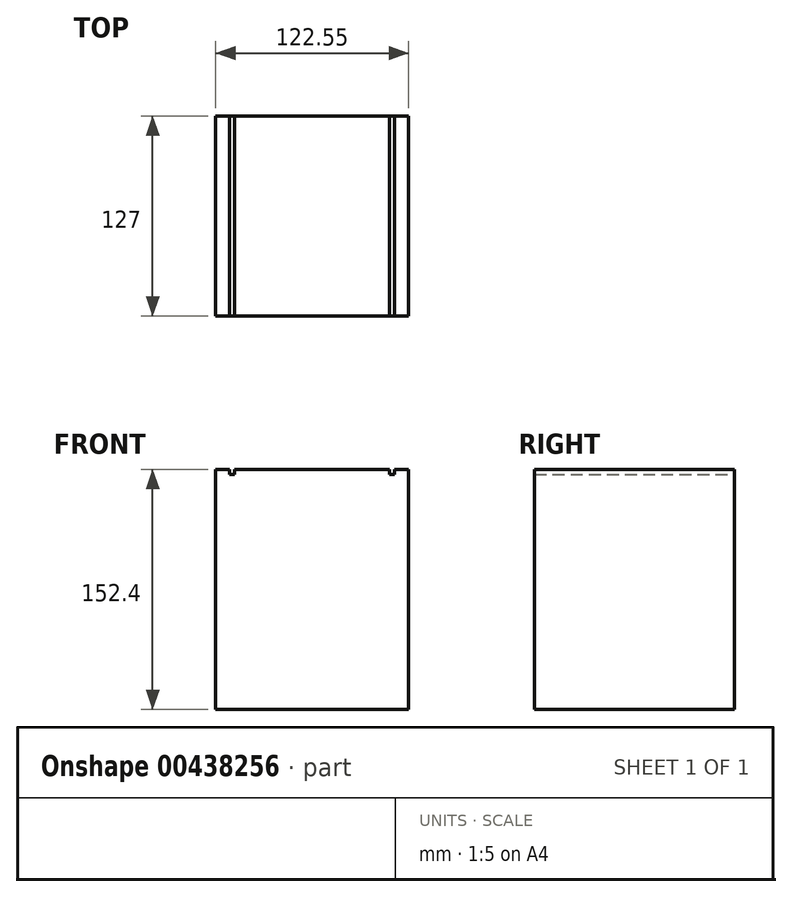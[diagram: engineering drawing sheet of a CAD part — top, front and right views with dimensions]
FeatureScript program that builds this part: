
annotation { "Feature Type Name" : "Feature", "Feature Type Description" : "" }
export const myFeature = defineFeature(function(context is Context, id is Id, definition is map)
    precondition{}
    {
        {
            var Q0;
            Q0=qCreatedBy(makeId("Front.planeOp"),FACE);
            var sketch = newSketch(context, id + "F0", { "sketchPlane" : qUnion([Q0])});
            skLineSegment(sketch, "E0.bottom", {"start": v(-65.18, 88) * mm, "end": v(-56.3, 88) * mm});
            skLineSegment(sketch, "E0.top", {"start": v(-65.18, -64.4) * mm, "end": v(57.37, -64.4) * mm});
            skLineSegment(sketch, "E0.left", {"start": v(-65.18, 88) * mm, "end": v(-65.18, -64.4) * mm});
            skLineSegment(sketch, "E0.right", {"start": v(57.37, 88) * mm, "end": v(57.37, -64.4) * mm});
            skLineSegment(sketch, "E1.top", {"start": v(-56.3, 84.82) * mm, "end": v(-53.12, 84.82) * mm});
            skLineSegment(sketch, "E1.left", {"start": v(-53.12, 88) * mm, "end": v(-53.12, 84.82) * mm});
            skLineSegment(sketch, "E1.right", {"start": v(-56.3, 88) * mm, "end": v(-56.3, 84.82) * mm});
            skLineSegment(sketch, "E2.top", {"start": v(45.3, 84.82) * mm, "end": v(48.48, 84.82) * mm});
            skLineSegment(sketch, "E2.left", {"start": v(45.3, 88) * mm, "end": v(45.3, 84.82) * mm});
            skLineSegment(sketch, "E2.right", {"start": v(48.48, 88) * mm, "end": v(48.48, 84.82) * mm});
            skLineSegment(sketch, "E3.trimOffspring", {"start": v(-53.12, 88) * mm, "end": v(45.3, 88) * mm});
            skLineSegment(sketch, "E4.trimOffspring", {"start": v(48.48, 88) * mm, "end": v(57.37, 88) * mm});
            skSolve(sketch);
        }
        {
            var Q0;
            Q0 = qSketchRegion(id + "F0", true);
            extrude(context, id + "F1", {"entities" : qUnion([Q0]), "depth" : 127 * mm});
        }
    });
